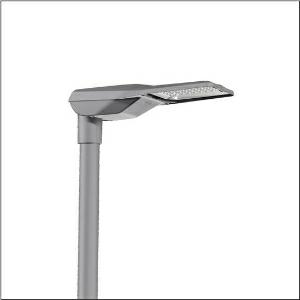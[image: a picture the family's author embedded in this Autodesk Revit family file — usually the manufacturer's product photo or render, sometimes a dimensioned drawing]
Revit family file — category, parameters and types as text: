
# Revit family: streetlight_sl_21_iq_mini___st1_0a_5xe2d41g08gb_82d1
name_source: partatom
category: Lighting Fixtures
units: mm (PartAtom-declared; Revit-internal decimal feet)

## family parameters
Cut with Voids When Loaded = No
Host = Face
Light Source = No
Part Type = Normal
Room Calculation Point = No
Round Connector Dimension = Use Diameter
Shared = No

## types (1)
- --- (1 x LED, 5920 lm, 37.1 W, 4000K)
    Apparent Load = 37 VA
    CIE Flux Codes = 37 72 97 100 100
    Color Rendering = 70
    Color Temperature = 4000K
    Default Elevation = 1800 mm
    Description = Streetlight SL 21 iQ mini, mast luminaire, primary light control with lens, of PMMA, primary optical cover: cover, of toughened safety glass, transparent, light distribution: ST1.0a, light emission: direct distribution, primary light characteristic: asymmetric, installation type: post-top, side-entry, LED, High Power LED, rated luminous flux: 5.920lm, luminous efficacy: 160lm/W, light colour: 740, colour temperature: 4000K, control gear: iQ Street-Remote, control: Street-Remote, Auto-Match, Temp-Guard, Lumen-Switch, Night-Set, Smart-Wire, Light-Fading, Desk-Remote (wireless, voltage-free reading and setting of iQ features in the workshop via application-optimized NFC function/RFID function), optimised constant luminous flux control (CLO 2.0), pre-setting: linear dimming characteristic, mains connection: 220..240V, AC, 50/60Hz, start of lifetime: 37W, end of service life: 39W, reduction: 18W, luminaire housing, of diecast aluminium, powder-coated, SITECO metallic grey (DB 702S), corrosivity category C5 high according to DIN EN ISO 12944, please order mast flange separately, inclination adjustable: 0°, 5°, 10°, 15°, sealing non-destructively replaceable, multi-level sealing system, length: 628mm, width: 235mm, height: 110mm, mast flange for spigot size: 42mm (side-entry): 5XC10008XM4, 60/48mm (side-entry/post-top): 5XC10108XM2, 76/60mm (side-entry/post-top): 5XC10108XM1, mounting height: 4..8m, protection rating (complete): IP66, insulation class (complete): insulation class II (safety insulation), certification: CE, ENEC, ENEC+, VDE, impact resistance: IK10, permissible operating ambient temperature for outdoor applications: -40..+50°C, standard-compliant lighting for roads and squares, packaging unit: 1 piece

Light Distribution: ST1.0a
    Height = 110 mm
    Lamp = 1 x LED
    Lamp Light Flux = 5920 lm
    Lamp Power = 37.1 W
    Lamp count = 1
    Length = 625 mm
    Luminous efficacy = 160 lm/W
    Manufacturer = Siteco
    ModVariant = No
    Model = 5XE2D41G08GB
    Number of Poles = 1
    OnlyDefault = Yes
    Power Factor = 1
    Product Name = Streetlight SL 21 iQ mini | ST1.0a
    Product group = mast luminaire | pylon top
    ProductGroupID = 6100
    Protection Class = Protection class II
    Protection Degree = IP 66
    RLX_Detail_Level = 1
    RLX_Emergency_Light_Flux = 0 lm
    RLX_Emergency_Type = 0
    RLX_Emergency_Type_DB = No
    RlxData = <blob elided: 26333 chars, md5=ac2795e7>
    Socket = socket
    Standby Power = 0 W
    System Light Flux = 5920 lm
    System Power = 37 W
    Type Comments = factory setting: luminous flux: 100 % | dim-lin: 254 | 385 mA
    Type Image = l_1003519.jpg
    URL = http://relux.com
    VarID = @adj_186305
    Voltage = 0 V
    Weight = 0.00 kg
    Width = 234 mm

## geometry (parser evidence)
native form markers: Blend x4, Sweep x10
no freeform markers — native parametric forms only
